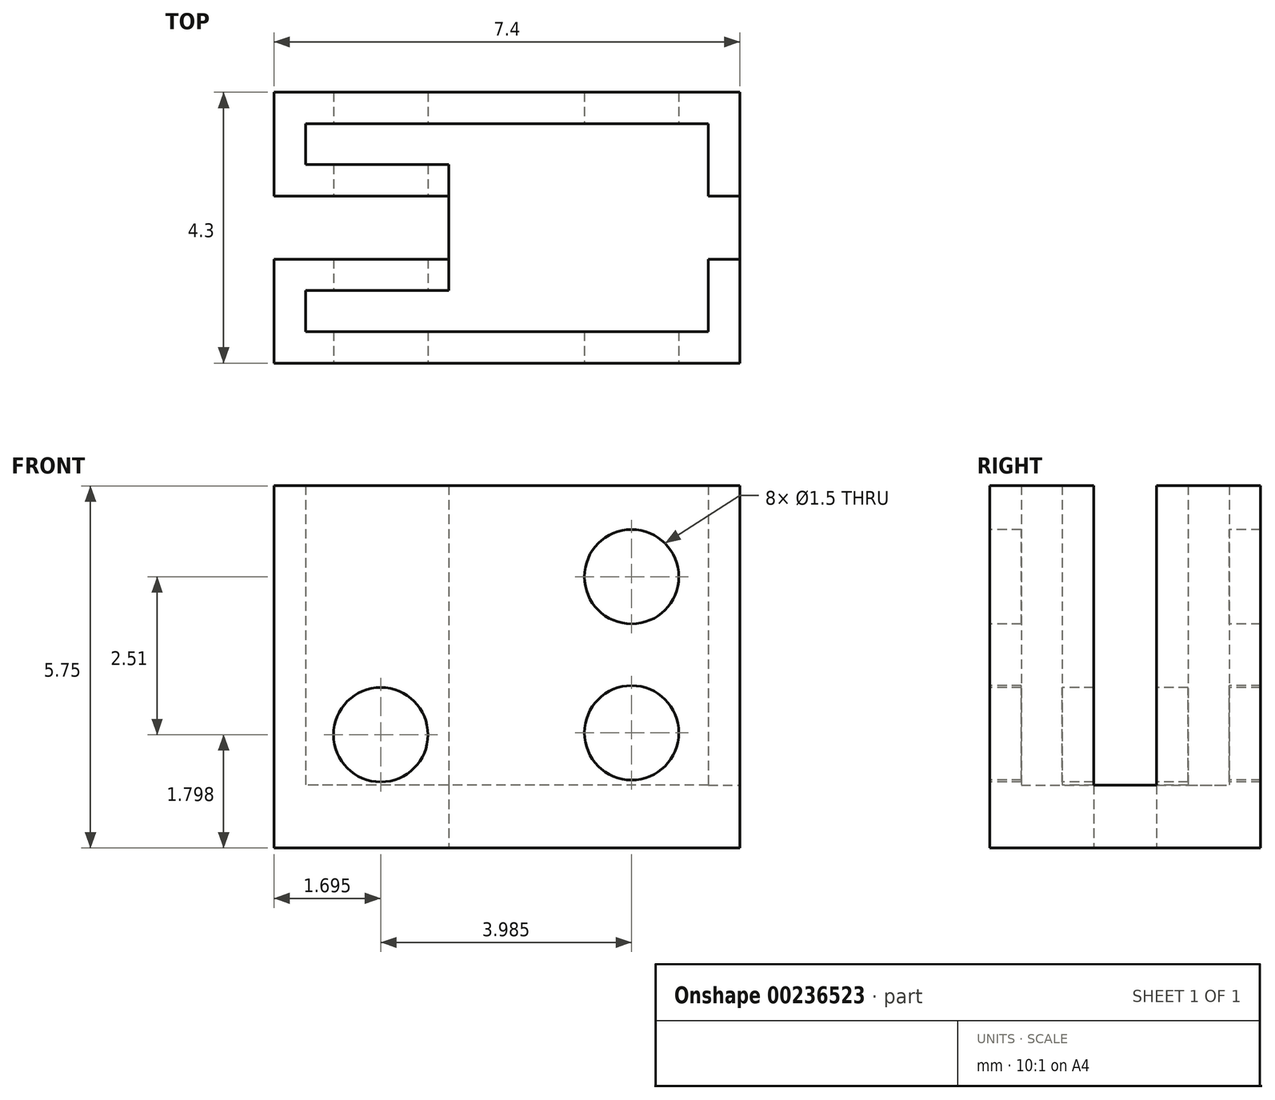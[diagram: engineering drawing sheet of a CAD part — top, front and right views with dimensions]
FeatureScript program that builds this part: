
annotation { "Feature Type Name" : "Feature", "Feature Type Description" : "" }
export const myFeature = defineFeature(function(context is Context, id is Id, definition is map)
    precondition{}
    {
        {
            var Q0;
            Q0=qCreatedBy(makeId("Top.planeOp"),FACE);
            var sketch = newSketch(context, id + "F0", { "sketchPlane" : qUnion([Q0])});
            skLineSegment(sketch, "E0.bottom", {"start": v(3.7, -2.15) * mm, "end": v(-3.7, -2.15) * mm});
            skLineSegment(sketch, "E0.top", {"start": v(3.7, 2.15) * mm, "end": v(-3.7, 2.15) * mm});
            skLineSegment(sketch, "E0.left", {"start": v(3.7, -2.15) * mm, "end": v(3.7, 2.15) * mm});
            skLineSegment(sketch, "E0.right", {"start": v(-3.7, -2.15) * mm, "end": v(-3.7, -0.5) * mm});
            skPoint(sketch, "E0.middle", {"position": v(0, 0) * mm});
            skLineSegment(sketch, "E1.trimOffspring", {"start": v(-3.7, 0.5) * mm, "end": v(-3.7, 2.15) * mm});
            skLineSegment(sketch, "E2", {"start": v(0.14, 0) * mm, "end": v(-3.7, 0) * mm, "construction": true});
            skLineSegment(sketch, "E3.0", {"start": v(-0.92, 0.5) * mm, "end": v(-3.7, 0.5) * mm});
            skLineSegment(sketch, "E4.0", {"start": v(-0.92, -0.5) * mm, "end": v(-3.7, -0.5) * mm});
            skLineSegment(sketch, "E5", {"start": v(-0.92, 1) * mm, "end": v(-0.92, -1) * mm});
            skLineSegment(sketch, "E6.0", {"start": v(3.2, 1.65) * mm, "end": v(-3.2, 1.65) * mm});
            skLineSegment(sketch, "E7.0", {"start": v(3.2, -1.65) * mm, "end": v(3.2, -0.5) * mm});
            skLineSegment(sketch, "E8.0", {"start": v(3.2, -1.65) * mm, "end": v(-3.2, -1.65) * mm});
            skLineSegment(sketch, "E9.0", {"start": v(-3.2, -1.65) * mm, "end": v(-3.2, -1) * mm});
            skLineSegment(sketch, "E10.0", {"start": v(-3.2, 1) * mm, "end": v(-3.2, 1.65) * mm});
            skLineSegment(sketch, "E11.0", {"start": v(-0.92, 1) * mm, "end": v(-3.2, 1) * mm});
            skLineSegment(sketch, "E12.0", {"start": v(-0.92, -1) * mm, "end": v(-3.2, -1) * mm});
            skLineSegment(sketch, "E13.MirrorCS", {"start": v(3.2, 0.5) * mm, "end": v(3.7, 0.5) * mm});
            skLineSegment(sketch, "E14.MirrorCS", {"start": v(3.2, -0.5) * mm, "end": v(3.7, -0.5) * mm});
            skPoint(sketch, "E15.orphan", {"position": v(0.92, 0.5) * mm});
            skLineSegment(sketch, "E16.trimOffspring", {"start": v(3.2, 0.5) * mm, "end": v(3.2, 1.65) * mm});
            skPoint(sketch, "E17.orphan", {"position": v(0.92, -0.5) * mm});
            skSolve(sketch);
        }
        {
            var Q0;
            Q0=makeQuery(id+"F0.imprint","IMPRINT",FACE,{"disambiguationData":[TD([[makeQuery(id+"F0.imprint","IMPRINT",EDGE,{"derivedFrom":sQuery(id+"F0.wireOp",EDGE,"E0.bottom")}),-1.0]])]});
            var Q1;
            {var subQ3=sQuery(id+"F0.wireOp",EDGE,"E0.top");Q1=makeQuery(id+"F0.imprint","IMPRINT",FACE,{"disambiguationData":[TD([[makeQuery(id+"F0.imprint","IMPRINT",EDGE,{"derivedFrom":subQ3}),1.0]])]});}
            extrude(context, id + "F1", {"entities" : qUnion([Q0, Q1]), "depth" : 5.75 * mm});
        }
        {
            var Q0;
            Q0=makeQuery(id+"F1.opExtrude","SWEPT_FACE",FACE,{"disambiguationData":[OSD([sQuery(id+"F0.wireOp",EDGE,"E0.bottom")])]});
            var sketch = newSketch(context, id + "F2", { "sketchPlane" : qUnion([Q0])});
            skCircle(sketch, "E18", {"center": v(1.98, 4.3) * mm, "radius": 0.75 * mm});
            skCircle(sketch, "E19", {"center": v(1.98, 1.83) * mm, "radius": 0.75 * mm});
            skCircle(sketch, "E20", {"center": v(-2, 1.8) * mm, "radius": 0.75 * mm});
            skLineSegment(sketch, "E21", {"start": v(1.98, 2.14) * mm, "end": v(-3.2, 2.14) * mm, "construction": true});
            skSolve(sketch);
        }
        {
            var Q0;
            Q0=makeQuery(id+"F2.imprint","IMPRINT",FACE,{"disambiguationData":[TD([[makeQuery(id+"F2.imprint","IMPRINT",EDGE,{"derivedFrom":sQuery(id+"F2.wireOp",EDGE,"E18")}),1.0]])]});
            var Q1;
            Q1=makeQuery(id+"F2.imprint","IMPRINT",FACE,{"disambiguationData":[TD([[makeQuery(id+"F2.imprint","IMPRINT",EDGE,{"derivedFrom":sQuery(id+"F2.wireOp",EDGE,"E19")}),1.0]])]});
            var Q2;
            Q2=makeQuery(id+"F2.imprint","IMPRINT",FACE,{"disambiguationData":[TD([[makeQuery(id+"F2.imprint","IMPRINT",EDGE,{"derivedFrom":sQuery(id+"F2.wireOp",EDGE,"E20")}),1.0]])]});
            extrude(context, id + "F3", {"entities" : qUnion([Q0, Q1, Q2]), "operationType" : NewBodyOperationType.REMOVE, "oppositeDirection" : true, "depth" : 25 * mm});
        }
        {
            var Q0;
            Q0=makeQuery(id+"F0.imprint","IMPRINT",FACE,{"disambiguationData":[TD([[makeQuery(id+"F0.imprint","IMPRINT",EDGE,{"derivedFrom":sQuery(id+"F0.wireOp",EDGE,"E6.0")}),1.0]])]});
            extrude(context, id + "F4", {"entities" : qUnion([Q0]), "operationType" : NewBodyOperationType.ADD, "depth" : 1 * mm});
        }
    });
